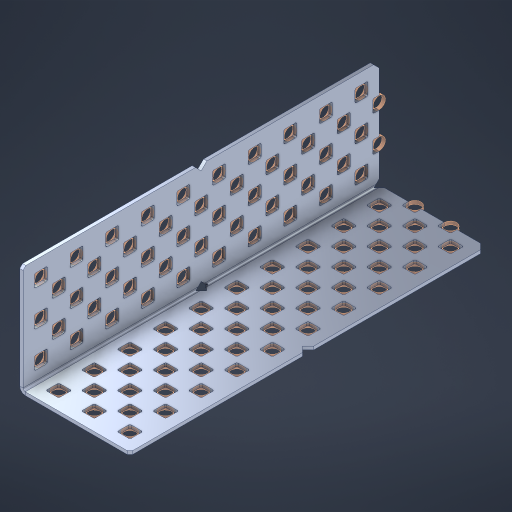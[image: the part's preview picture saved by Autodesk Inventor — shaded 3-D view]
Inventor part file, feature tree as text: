
AUTODESK INVENTOR PART (.ipt)
format: ipt  version: 2023 (Build 270158000, 158)  size: 1,321,984 bytes
history: native  units: in
note: dims shown in document units (in); Inventor stores cm internally (conversion verified against a paired STEP export)
features: other x106, extrude x98, sheet_metal_op x8, sketch x7, pattern_linear x3, mirror x1, chamfer x1
ambient origin geometry x8: Origin, YZ Plane, XZ Plane, XY Plane, X Axis, Y Axis, Z Axis, Center Point
bodies: Solid1 (feature_tree), Body (feature_tree)
feature tree (224):
  sheet_metal_op  "Flanges"
  sheet_metal_op  "Body Pattern"
  pattern_linear  "Center Double"  Spacing1=1.5in  [1 undecoded]
  pattern_linear  "Center Pattern"  Spacing1=0.1875in  [1 undecoded]
  other  "Arc Length"
  pattern_linear  "Notch Pattern"  Spacing1=0.0469in  [1 undecoded]
  other  "Diagonal Plane"
  mirror  "Everything Mirrored"
  chamfer  "End Chamfer"
  sketch  "Sketch1"  dims[d0=1.5in]
  other  "Plate1"
  sketch  "Sketch2"  dims[d1=5.0in]
  other  "Plate2"
  sheet_metal_op  "Bend1"
  sheet_metal_op  "Corner1"
  sketch  "Sketch8"  dims[d2=0.0469in]
  sketch  "Sketch9"  dims[d3=0.0469in]
  other  "Srf91"
  sheet_metal_op  "Body Pattern Sketch"
  other  "Srf92"
  sketch  "Sketch13"  dims[d4=0.0234in]
  sketch  "Sketch15"  dims[d5=0.0938in]
  sketch  "Sketch16"  dims[d6=0.0469in d7=1.5in d8=90.0deg d9=0.0312in d10=0.1875in d11=0.0469in d12=0.0469in d49=0.182in d50=0.02in d52=0.25in d53=0.0469in d54=0.0in d55=0.172in d56=1.0in d57=0.0in d85=0.1473in d86=0.1659in d89=0.0469in d90=0.0in d91=0.04in d92=0.0491in d95=2.5in d96=0.04in d97=0.25in d98=45.0deg d106=0.182in d107=0.02in d110=0.0469in d111=0.0in d112=0.172in d113=0.5in d114=0.0in d117=0.5in d126=0.0491in d127=0.1227in d128=0.08in d129=0.04in d130=2.5in d131=0.25in d132=3.937in d134=0.5in d135=1.1811in d137=0.5in d140=0.5in d141=1.0in d142=0.3937in d144=0.5in d145=0.071in d146=0.7874in d148=0.5in]
  other  "Srf786"
  other  "Srf856"
  other  "Srf889"
  other  "Srf890"
  other  "Srf891"
  other  "Srf1275"
  other  "Srf1276"
  other  "Srf1278"
  other  "Srf1277"
  other  "Srf1285"
  other  "Srf1286"
  other  "Srf1287"
  other  "Srf1445"
  other  "Srf1446"
  other  "Srf1447"
  other  "Srf1448"
  other  "Srf1449"
  other  "Srf1537"
  other  "Srf1538"
  other  "Srf1539"
  other  "Srf1540"
  other  "Srf1541"
  other  "Srf1807"
  other  "Srf1959"
  other  "Srf2009"
  other  "Srf2010"
  other  "Srf2011"
  other  "Srf2012"
  other  "Srf2013"
  other  "Srf2014"
  other  "Srf2015"
  other  "Srf2016"
  other  "Srf2017"
  other  "Srf2018"
  other  "Srf2043"
  other  "Srf2044"
  other  "Srf2045"
  other  "Srf2046"
  other  "Srf2047"
  other  "Srf2048"
  other  "Srf2049"
  other  "Srf2050"
  other  "Srf2051"
  other  "Srf2076"
  other  "Srf2077"
  other  "Srf2078"
  other  "Srf2079"
  other  "Srf2080"
  other  "Srf2081"
  other  "Srf2082"
  other  "Srf2083"
  other  "Srf2084"
  other  "Srf2085"
  other  "Srf2086"
  other  "Srf2087"
  other  "Srf2088"
  other  "Srf2089"
  other  "Srf2090"
  other  "Srf2091"
  other  "Srf2092"
  other  "Srf2093"
  other  "Srf2094"
  other  "Srf2095"
  other  "Srf2096"
  other  "Srf2097"
  other  "Srf2098"
  other  "Srf2099"
  other  "Srf2100"
  other  "Srf2101"
  other  "Srf2102"
  other  "Srf2103"
  other  "Srf2179"
  other  "Srf2180"
  other  "Srf2181"
  other  "Srf2182"
  other  "Srf2183"
  other  "Srf2184"
  other  "Srf2185"
  other  "Srf2186"
  other  "Srf2187"
  other  "Srf2188"
  other  "Srf2189"
  other  "Srf2190"
  other  "Srf2191"
  other  "Srf2192"
  other  "Srf2193"
  other  "Srf2194"
  other  "Srf2195"
  other  "Srf2196"
  other  "Srf2197"
  other  "Srf2198"
  other  "Srf2199"
  other  "Srf2200"
  other  "Srf2201"
  other  "Srf2202"
  other  "Srf2203"
  other  "Srf2204"
  other  "Srf2205"
  sheet_metal_op  "Body Stamp"
  sheet_metal_op  "Body Circle"
  other  "Center Stamp"
  other  "Center Circle"
  sheet_metal_op  "Notch"
  extrude  "ExtrusionSrf92"  Depth=0.0469in
  extrude  "ExtrusionSrf856"  Depth=0.3937in
  extrude  "ExtrusionSrf889"  Depth=0.02in
  extrude  "ExtrusionSrf890"  Depth=0.25in
  extrude  "ExtrusionSrf891"  Depth=0.0469in
  extrude  "ExtrusionSrf1275"  TaperAngle=0.0deg  [1 undecoded]
  extrude  "ExtrusionSrf1276"  Depth=0.3937in
  extrude  "ExtrusionSrf1277"  Depth=0.3937in TaperAngle=0.0deg
  extrude  "ExtrusionSrf1345"  Depth=0.3937in
  extrude  "ExtrusionSrf1346"  Depth=0.3937in
  extrude  "ExtrusionSrf1347"  Depth=0.0469in
  extrude  "ExtrusionSrf1348"  Depth=0.3937in TaperAngle=0.0deg
  extrude  "ExtrusionSrf1445"  Depth=2.5in
  extrude  "ExtrusionSrf1446"  Depth=0.25in TaperAngle=45.0deg
  extrude  "ExtrusionSrf1447"  Depth=0.3937in
  extrude  "ExtrusionSrf1448"  Depth=0.02in
  extrude  "ExtrusionSrf1449"  Depth=0.0469in
  extrude  "ExtrusionSrf1537"  TaperAngle=0.0deg  [1 undecoded]
  extrude  "ExtrusionSrf1538"  Depth=0.3937in
  extrude  "ExtrusionSrf1539"  Depth=0.3937in TaperAngle=0.0deg
  extrude  "ExtrusionSrf1540"  Depth=0.3937in
  extrude  "ExtrusionSrf1541"  Depth=0.3937in
  extrude  "ExtrusionSrf1807"  Depth=0.3937in
  extrude  "ExtrusionSrf1959"  Depth=0.3937in
  extrude  "ExtrusionSrf2009"  Depth=0.3937in
  extrude  "ExtrusionSrf2010"  Depth=2.5in
  extrude  "ExtrusionSrf2011"  Depth=0.25in
  extrude  "ExtrusionSrf2012"  Depth=0.3937in
  extrude  "ExtrusionSrf2013"  Depth=0.3937in
  extrude  "ExtrusionSrf2014"  Depth=0.3937in
  extrude  "ExtrusionSrf2015"  Depth=0.3937in
  extrude  "ExtrusionSrf2016"  Depth=0.3937in
  extrude  "ExtrusionSrf2017"  Depth=0.3937in
  extrude  "ExtrusionSrf2018"  Depth=0.3937in
  extrude  "ExtrusionSrf2043"  [1 undecoded]
  extrude  "ExtrusionSrf2044"  [1 undecoded]
  extrude  "ExtrusionSrf2045"  [1 undecoded]
  extrude  "ExtrusionSrf2046"  [1 undecoded]
  extrude  "ExtrusionSrf2047"  [1 undecoded]
  extrude  "ExtrusionSrf2048"  [1 undecoded]
  extrude  "ExtrusionSrf2049"  [1 undecoded]
  extrude  "ExtrusionSrf2050"  [1 undecoded]
  extrude  "ExtrusionSrf2051"  [1 undecoded]
  extrude  "ExtrusionSrf2076"  [1 undecoded]
  extrude  "ExtrusionSrf2077"  [1 undecoded]
  extrude  "ExtrusionSrf2078"  [1 undecoded]
  extrude  "ExtrusionSrf2079"  [1 undecoded]
  extrude  "ExtrusionSrf2080"  [1 undecoded]
  extrude  "ExtrusionSrf2081"  [1 undecoded]
  extrude  "ExtrusionSrf2082"  [1 undecoded]
  extrude  "ExtrusionSrf2083"  [1 undecoded]
  extrude  "ExtrusionSrf2084"  [1 undecoded]
  extrude  "ExtrusionSrf2085"  [1 undecoded]
  extrude  "ExtrusionSrf2086"  [1 undecoded]
  extrude  "ExtrusionSrf2087"  [1 undecoded]
  extrude  "ExtrusionSrf2088"  [1 undecoded]
  extrude  "ExtrusionSrf2089"  [1 undecoded]
  extrude  "ExtrusionSrf2090"  [1 undecoded]
  extrude  "ExtrusionSrf2091"  [1 undecoded]
  extrude  "ExtrusionSrf2092"  [1 undecoded]
  extrude  "ExtrusionSrf2093"  [1 undecoded]
  extrude  "ExtrusionSrf2094"  [1 undecoded]
  extrude  "ExtrusionSrf2095"  [1 undecoded]
  extrude  "ExtrusionSrf2096"  [1 undecoded]
  extrude  "ExtrusionSrf2097"  [1 undecoded]
  extrude  "ExtrusionSrf2098"  [1 undecoded]
  extrude  "ExtrusionSrf2099"  [1 undecoded]
  extrude  "ExtrusionSrf2100"  [1 undecoded]
  extrude  "ExtrusionSrf2101"  [1 undecoded]
  extrude  "ExtrusionSrf2102"  [1 undecoded]
  extrude  "ExtrusionSrf2103"  [1 undecoded]
  extrude  "ExtrusionSrf2179"  [1 undecoded]
  extrude  "ExtrusionSrf2180"  [1 undecoded]
  extrude  "ExtrusionSrf2181"  [1 undecoded]
  extrude  "ExtrusionSrf2182"  [1 undecoded]
  extrude  "ExtrusionSrf2183"  [1 undecoded]
  extrude  "ExtrusionSrf2184"  [1 undecoded]
  extrude  "ExtrusionSrf2185"  [1 undecoded]
  extrude  "ExtrusionSrf2186"  [1 undecoded]
  extrude  "ExtrusionSrf2187"  [1 undecoded]
  extrude  "ExtrusionSrf2188"  [1 undecoded]
  extrude  "ExtrusionSrf2189"  [1 undecoded]
  extrude  "ExtrusionSrf2190"  [1 undecoded]
  extrude  "ExtrusionSrf2191"  [1 undecoded]
  extrude  "ExtrusionSrf2192"  [1 undecoded]
  extrude  "ExtrusionSrf2193"  [1 undecoded]
  extrude  "ExtrusionSrf2194"  [1 undecoded]
  extrude  "ExtrusionSrf2195"  [1 undecoded]
  extrude  "ExtrusionSrf2196"  [1 undecoded]
  extrude  "ExtrusionSrf2197"  [1 undecoded]
  extrude  "ExtrusionSrf2198"  [1 undecoded]
  extrude  "ExtrusionSrf2199"  [1 undecoded]
  extrude  "ExtrusionSrf2200"  [1 undecoded]
  extrude  "ExtrusionSrf2201"  [1 undecoded]
  extrude  "ExtrusionSrf2202"  [1 undecoded]
  extrude  "ExtrusionSrf2203"  [1 undecoded]
  extrude  "ExtrusionSrf2204"  [1 undecoded]
  extrude  "ExtrusionSrf2205"  [1 undecoded]
note: 69 required parameter values undecoded (feature->parameter linkage not recoverable at this tier; creation-order binding heuristic only, values carry confidence <= 0.55)
